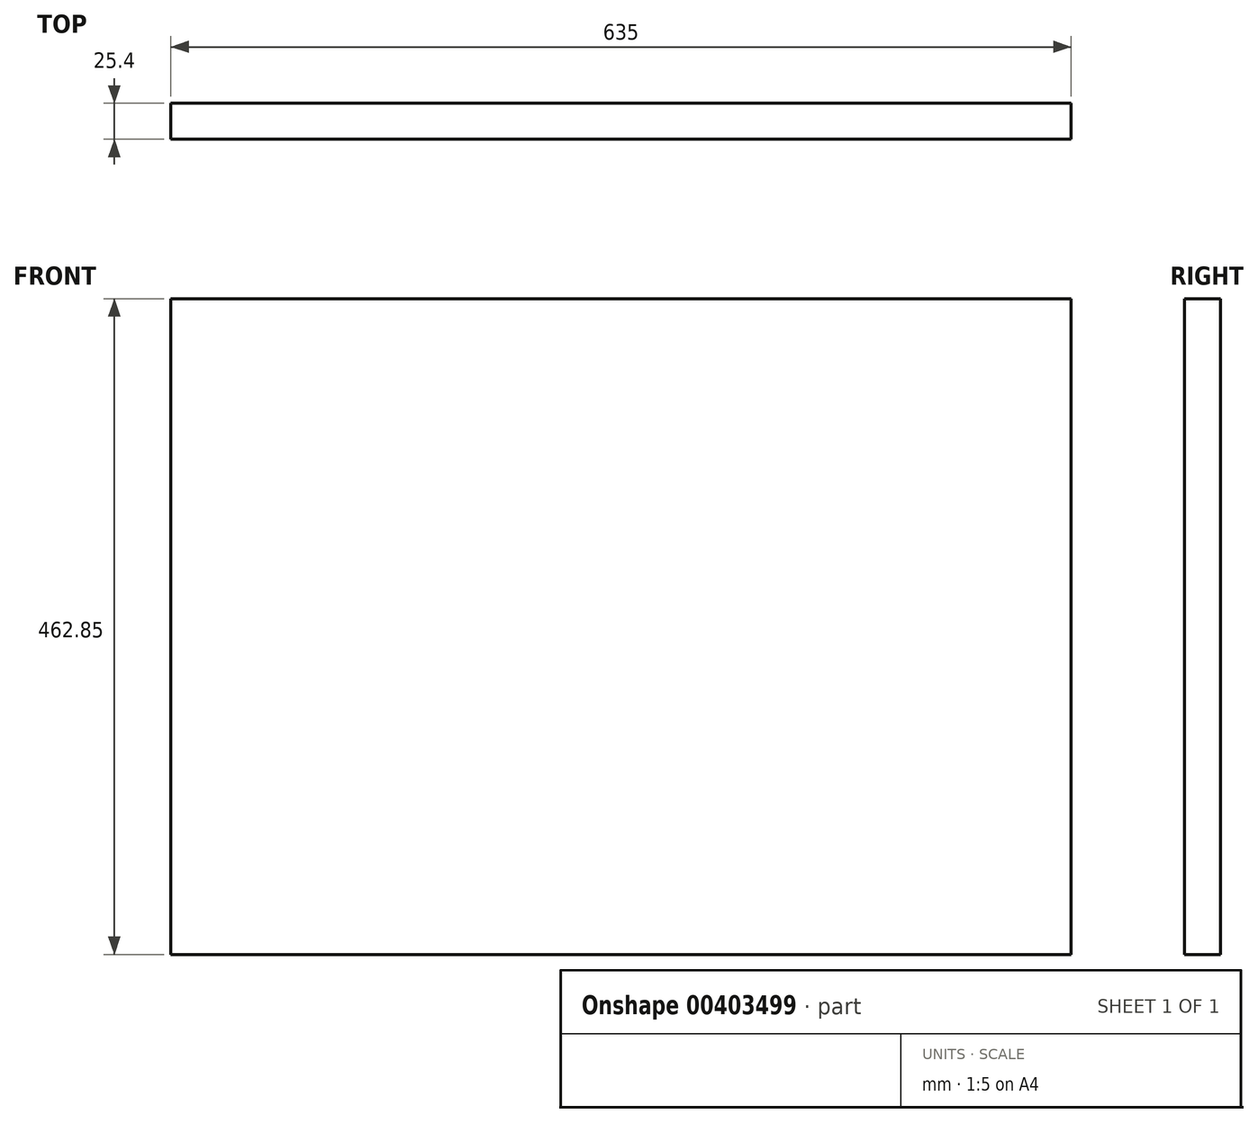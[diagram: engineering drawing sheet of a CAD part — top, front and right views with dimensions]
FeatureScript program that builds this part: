
annotation { "Feature Type Name" : "Feature", "Feature Type Description" : "" }
export const myFeature = defineFeature(function(context is Context, id is Id, definition is map)
    precondition{}
    {
        {
            var Q0;
            Q0=qCreatedBy(makeId("Front.planeOp"),FACE);
            var sketch = newSketch(context, id + "F0", { "sketchPlane" : qUnion([Q0])});
            skLineSegment(sketch, "E0.bottom", {"start": v(-324.05, 241.6) * mm, "end": v(310.95, 241.6) * mm});
            skLineSegment(sketch, "E0.top", {"start": v(-324.05, -221.25) * mm, "end": v(310.95, -221.25) * mm});
            skLineSegment(sketch, "E0.left", {"start": v(-324.05, 241.6) * mm, "end": v(-324.05, -221.25) * mm});
            skLineSegment(sketch, "E0.right", {"start": v(310.95, 241.6) * mm, "end": v(310.95, -221.25) * mm});
            skSolve(sketch);
        }
        {
            var Q0;
            Q0 = qSketchRegion(id + "F0", true);
            extrude(context, id + "F1", {"entities" : qUnion([Q0]), "depth" : 25.4 * mm});
        }
    });
